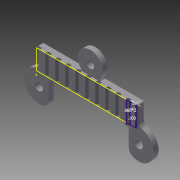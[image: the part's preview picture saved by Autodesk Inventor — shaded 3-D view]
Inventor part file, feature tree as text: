
AUTODESK INVENTOR PART (.ipt)
format: ipt  version: 2013 SP2 (Build 170200200, 200)  size: 330,240 bytes
history: native  units: in
note: dims shown in document units (in); Inventor stores cm internally (conversion verified against a paired STEP export)
features: sketch x12, extrude x11, fillet x6
ambient origin geometry x8: Origin, YZ Plane, XZ Plane, XY Plane, X Axis, Y Axis, Z Axis, Center Point
bodies: Solid1 (feature_tree)
feature tree (29):
  extrude  "Extrusion1"  Depth=0.16in
  fillet  "Fillet5"  Radius=0.4in
  fillet  "Fillet6"  Radius=2.0in
  extrude  "Extrusion2"  Depth=0.125in
  sketch  "Sketch3"  dims[d40=0.125in d43=2.0in]
  extrude  "Extrusion3"  Depth=2.0in
  extrude  "Extrusion4"  Depth=0.14in
  extrude  "Extrusion6"  Depth=0.02in
  extrude  "Extrusion7"  Depth=0.02in
  extrude  "Extrusion8"  Depth=0.14in
  extrude  "Extrusion9"  Depth=0.06in
  extrude  "Extrusion10"  Depth=0.06in
  extrude  "Extrusion11"  Depth=0.06in
  extrude  "Extrusion12"  Depth=0.06in
  fillet  "Fillet7"  Radius=0.06in
  fillet  "Fillet8"  Radius=0.06in
  fillet  "Fillet9"  Radius=1.0in
  fillet  "Fillet10"  Radius=1.5in
  sketch  "Sketch1"  dims[d28=0.4693in d29=0.16in d30=0.4in d31=2.0in]
  sketch  "Sketch2"  dims[d33=0.25in d34=0.0in d39=0.125in]
  sketch  "Sketch4"  dims[d69=0.049in d70=0.0in d71=0.14in]
  sketch  "Sketch5"  dims[d72=0.06in d73=0.02in]
  sketch  "Sketch9"  dims[d74=0.1in d75=0.02in]
  sketch  "Sketch10"  dims[d76=1.0in d77=0.0in d78=0.14in]
  sketch  "Sketch11"  dims[d80=0.06in d82=0.06in]
  sketch  "Sketch12"  dims[d83=0.06in d84=0.06in]
  sketch  "Sketch13"  dims[d85=0.06in d86=0.06in]
  sketch  "Sketch14"  dims[d87=0.06in d88=0.06in d89=0.06in d90=0.06in d91=1.0in d92=0.0in d100=1.5in]
  sketch  "Sketch15"  dims[d102=0.2in d103=90.0deg d105=0.16in d107=0.25in d108=0.0in d109=0.3333in d110=0.0in d111=0.15in d112=0.0in d113=0.1in d114=0.0in d115=1.0in d116=0.0in d117=0.1in d118=0.0in d119=1.0in d120=0.0in d121=0.125in d122=0.125in d123=0.125in d124=0.125in d125=0.3in d126=0.3in]
